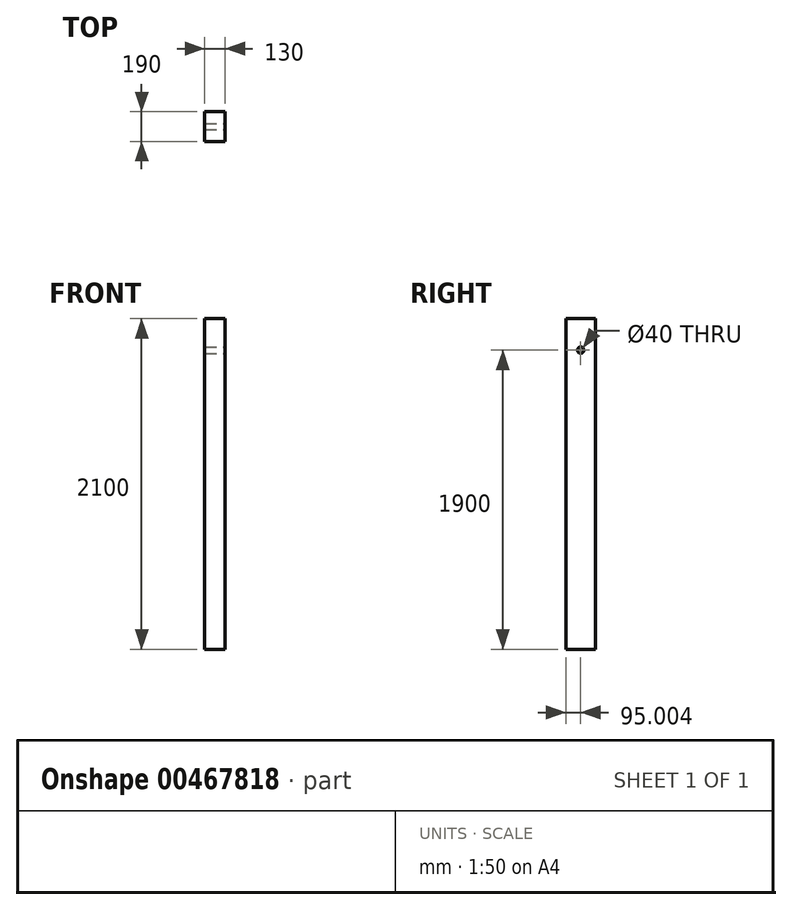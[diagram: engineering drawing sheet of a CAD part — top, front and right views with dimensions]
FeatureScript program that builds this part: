
annotation { "Feature Type Name" : "Feature", "Feature Type Description" : "" }
export const myFeature = defineFeature(function(context is Context, id is Id, definition is map)
    precondition{}
    {
        {
            var Q0;
            Q0=qCreatedBy(makeId("Top.planeOp"),FACE);
            var sketch = newSketch(context, id + "F0", { "sketchPlane" : qUnion([Q0])});
            skLineSegment(sketch, "E0.bottom", {"start": v(-65, 181.65) * mm, "end": v(65, 181.65) * mm});
            skLineSegment(sketch, "E0.top", {"start": v(-65, -8.35) * mm, "end": v(65, -8.35) * mm});
            skLineSegment(sketch, "E0.left", {"start": v(-65, 181.65) * mm, "end": v(-65, -8.35) * mm});
            skLineSegment(sketch, "E0.right", {"start": v(65, 181.65) * mm, "end": v(65, -8.35) * mm});
            skPoint(sketch, "E0.middle", {"position": v(0, 86.65) * mm});
            skLineSegment(sketch, "E1.bottom", {"start": v(34.26, 181.65) * mm, "end": v(-34.26, 181.65) * mm});
            skLineSegment(sketch, "E1.top", {"start": v(34.26, 181.65) * mm, "end": v(-34.26, 181.65) * mm});
            skLineSegment(sketch, "E1.left", {"start": v(34.26, 181.65) * mm, "end": v(34.26, 181.65) * mm});
            skLineSegment(sketch, "E1.right", {"start": v(-34.26, 181.65) * mm, "end": v(-34.26, 181.65) * mm});
            skPoint(sketch, "E1.middle", {"position": v(0, 181.65) * mm});
            skSolve(sketch);
        }
        {
            var Q0;
            Q0=makeQuery(id+"F0.imprint","IMPRINT",FACE,{"disambiguationData":[TD([[makeQuery(id+"F0.imprint","IMPRINT",EDGE,{"derivedFrom":sQuery(id+"F0.wireOp",EDGE,"E0.top")}),1.0]])]});
            extrude(context, id + "F1", {"entities" : qUnion([Q0]), "depth" : 2100 * mm});
        }
        {
            var Q0;
            Q0=makeQuery(id+"F1.opExtrude","SWEPT_FACE",FACE,{"disambiguationData":[OSD([sQuery(id+"F0.wireOp",EDGE,"E0.right")])]});
            var sketch = newSketch(context, id + "F2", { "sketchPlane" : qUnion([Q0])});
            skCircle(sketch, "E2", {"center": v(86.65, 1900) * mm, "radius": 20 * mm});
            skSolve(sketch);
        }
        {
            var Q0;
            Q0=sQuery(id+"F2.wireOp",VERTEX,"E2.center");
            var Q1;
            Q1=makeQuery(id+"F1.opExtrude","SWEPT_BODY",BODY,{"disambiguationData":[OSD([sQuery(id+"F0.wireOp",EDGE,"E0.bottom"),sQuery(id+"F0.wireOp",EDGE,"E0.top"),sQuery(id+"F0.wireOp",EDGE,"E0.left"),sQuery(id+"F0.wireOp",EDGE,"E0.right"),sQuery(id+"F0.wireOp",EDGE,"E1.top")])]});
            hole(context, id + "F3", {"style" : HoleStyle.SIMPLE, "endStyle" : HoleEndStyle.THROUGH, "holeDiameter" : 40 * mm, "isTappedThrough" : true, "tappedDepth" : 12 * mm, "tapClearance" : 3, "locations" : qUnion([Q0]), "scope" : qUnion([Q1])});
        }
    });
